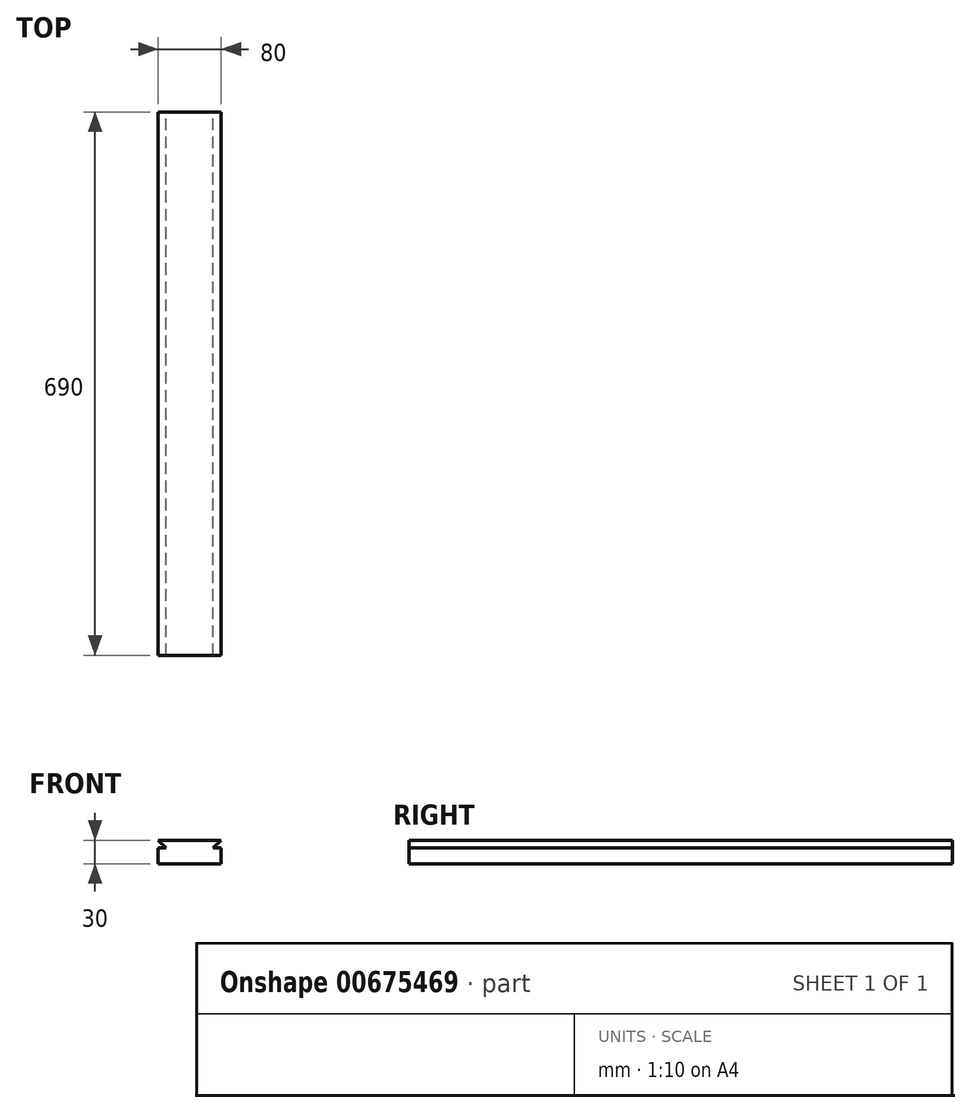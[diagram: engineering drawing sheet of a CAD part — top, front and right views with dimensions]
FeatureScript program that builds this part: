
annotation { "Feature Type Name" : "Feature", "Feature Type Description" : "" }
export const myFeature = defineFeature(function(context is Context, id is Id, definition is map)
    precondition{}
    {
        {
            var Q0;
            Q0=qCreatedBy(makeId("Front.planeOp"),FACE);
            var sketch = newSketch(context, id + "F0", { "sketchPlane" : qUnion([Q0])});
            skLineSegment(sketch, "E0", {"start": v(-103.1, 28.12) * mm, "end": v(-23.1, 28.12) * mm});
            skLineSegment(sketch, "E1", {"start": v(-23.1, 28.12) * mm, "end": v(-33.1, 18.12) * mm});
            skLineSegment(sketch, "E2", {"start": v(-33.1, 18.12) * mm, "end": v(-23.1, 18.12) * mm});
            skLineSegment(sketch, "E3", {"start": v(-23.1, 18.12) * mm, "end": v(-23.1, -1.88) * mm});
            skLineSegment(sketch, "E4", {"start": v(-23.1, -1.88) * mm, "end": v(-103.1, -1.88) * mm});
            skLineSegment(sketch, "E5", {"start": v(-103.1, -1.88) * mm, "end": v(-103.1, 18.12) * mm});
            skLineSegment(sketch, "E6", {"start": v(-103.1, 18.12) * mm, "end": v(-93.1, 18.12) * mm});
            skLineSegment(sketch, "E7", {"start": v(-93.1, 18.12) * mm, "end": v(-103.1, 28.12) * mm});
            skSolve(sketch);
        }
        {
            var Q0;
            Q0 = qSketchRegion(id + "F0", true);
            extrude(context, id + "F1", {"entities" : qUnion([Q0]), "depth" : 690 * mm, "offsetDistance" : 25 * mm});
        }
    });
